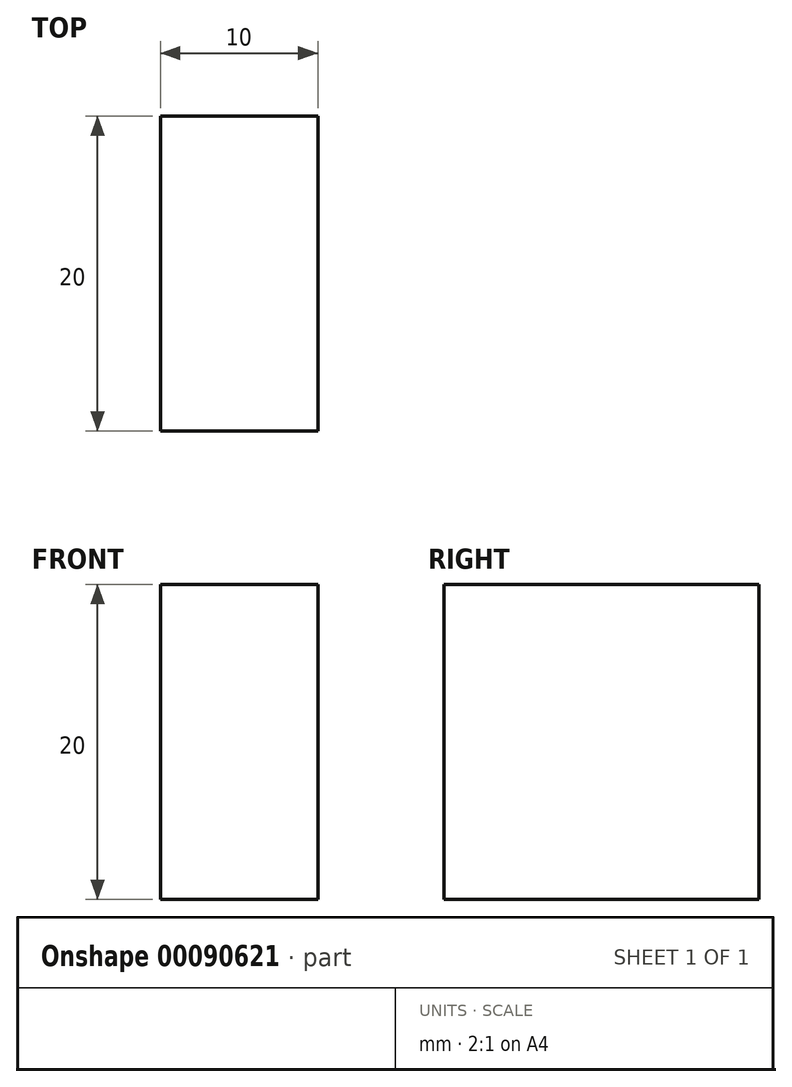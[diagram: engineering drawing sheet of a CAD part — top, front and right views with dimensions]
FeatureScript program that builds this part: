
annotation { "Feature Type Name" : "Feature", "Feature Type Description" : "" }
export const myFeature = defineFeature(function(context is Context, id is Id, definition is map)
    precondition{}
    {
        {
            var Q0;
            Q0=qCreatedBy(makeId("Top.planeOp"),FACE);
            var sketch = newSketch(context, id + "F0", { "sketchPlane" : qUnion([Q0])});
            skLineSegment(sketch, "E0.bottom", {"start": v(-46.86, -19.16) * mm, "end": v(-36.86, -19.16) * mm});
            skLineSegment(sketch, "E0.top", {"start": v(-46.86, -39.16) * mm, "end": v(-36.86, -39.16) * mm});
            skLineSegment(sketch, "E0.left", {"start": v(-46.86, -19.16) * mm, "end": v(-46.86, -39.16) * mm});
            skLineSegment(sketch, "E0.right", {"start": v(-36.86, -19.16) * mm, "end": v(-36.86, -39.16) * mm});
            skSolve(sketch);
        }
        {
            var Q0;
            Q0=makeQuery(id+"F0.imprint","IMPRINT",FACE,{"disambiguationData":[TD([[makeQuery(id+"F0.imprint","IMPRINT",EDGE,{"derivedFrom":sQuery(id+"F0.wireOp",EDGE,"E0.bottom")}),-1.0]])]});
            extrude(context, id + "F1", {"entities" : qUnion([Q0]), "depth" : 20 * mm});
        }
    });
